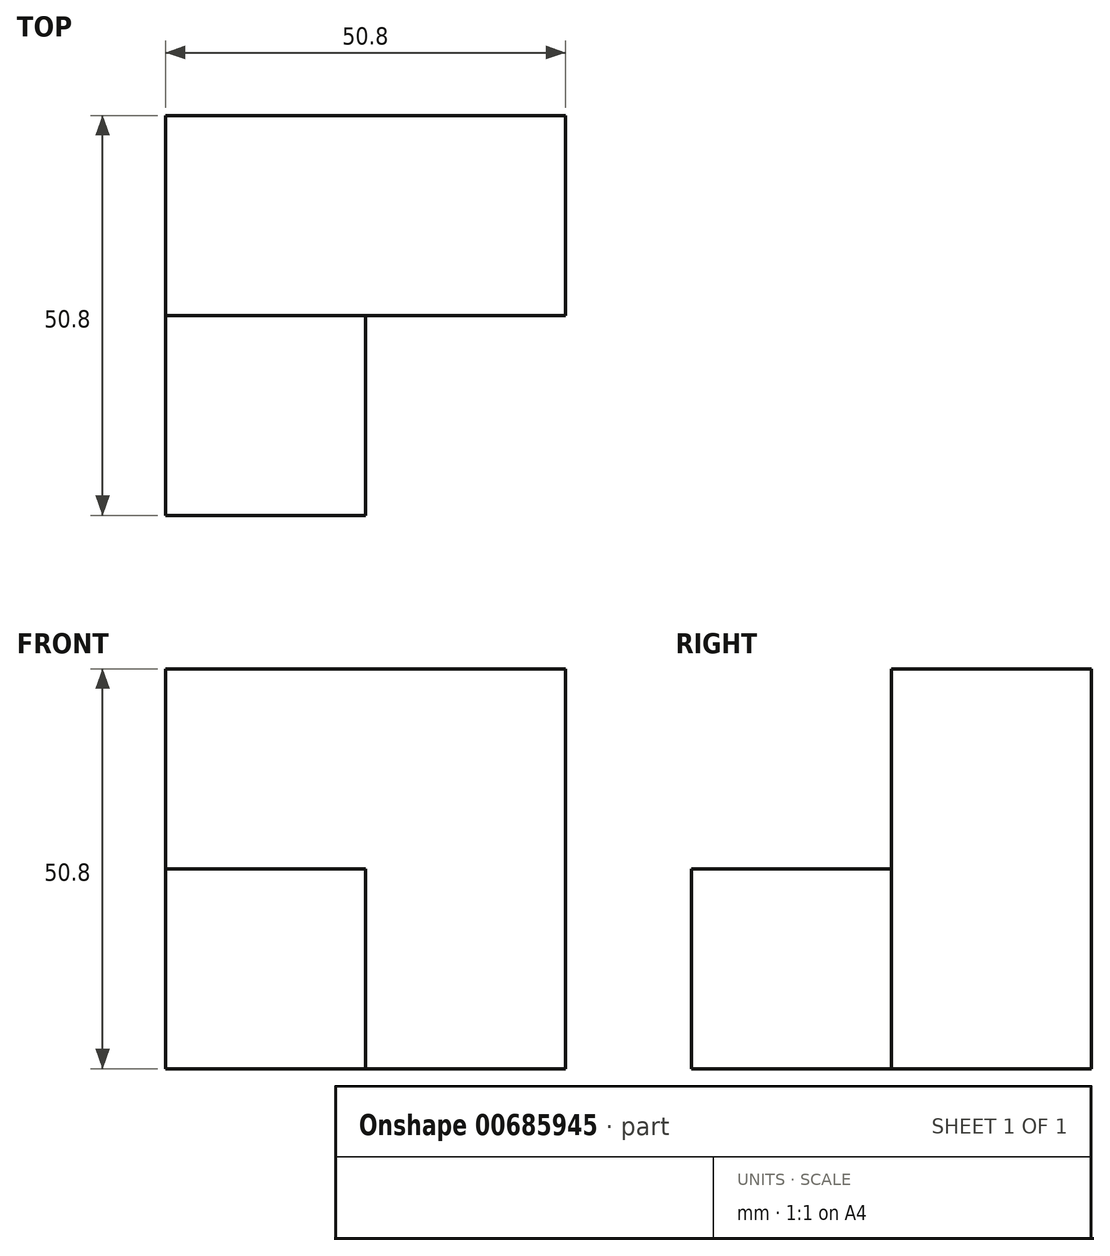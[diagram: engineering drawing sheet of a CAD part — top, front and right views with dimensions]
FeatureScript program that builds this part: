
annotation { "Feature Type Name" : "Feature", "Feature Type Description" : "" }
export const myFeature = defineFeature(function(context is Context, id is Id, definition is map)
    precondition{}
    {
        {
            var Q0;
            Q0=qCreatedBy(makeId("Front.planeOp"),FACE);
            var sketch = newSketch(context, id + "F0", { "sketchPlane" : qUnion([Q0])});
            skLineSegment(sketch, "E0.bottom", {"start": v(0, 0) * mm, "end": v(-50.8, 0) * mm});
            skLineSegment(sketch, "E0.top", {"start": v(0, 50.8) * mm, "end": v(-50.8, 50.8) * mm});
            skLineSegment(sketch, "E0.left", {"start": v(0, 0) * mm, "end": v(0, 50.8) * mm});
            skLineSegment(sketch, "E0.right", {"start": v(-50.8, 0) * mm, "end": v(-50.8, 50.8) * mm});
            skLineSegment(sketch, "E1", {"start": v(0, 50.8) * mm, "end": v(0, 50.8) * mm});
            skSolve(sketch);
        }
        {
            var Q0;
            Q0=makeQuery(id+"F0.imprint","IMPRINT",FACE,{"disambiguationData":[TD([[makeQuery(id+"F0.imprint","IMPRINT",EDGE,{"derivedFrom":sQuery(id+"F0.wireOp",EDGE,"E0.bottom")}),-1.0]])]});
            extrude(context, id + "F1", {"entities" : qUnion([Q0]), "depth" : 25.4 * mm, "offsetDistance" : 25.4 * mm});
        }
        {
            var Q0;
            Q0=makeQuery(id+"F1.opExtrude","CAP_FACE",FACE,{"disambiguationData":[OSD([sQuery(id+"F0.wireOp",EDGE,"E0.bottom"),sQuery(id+"F0.wireOp",EDGE,"E0.top"),sQuery(id+"F0.wireOp",EDGE,"E0.left"),sQuery(id+"F0.wireOp",EDGE,"E0.right")])],"isStart":false});
            var sketch = newSketch(context, id + "F2", { "sketchPlane" : qUnion([Q0])});
            skLineSegment(sketch, "E2.bottom", {"start": v(-50.8, 0) * mm, "end": v(-25.4, 0) * mm});
            skLineSegment(sketch, "E2.top", {"start": v(-50.8, 25.4) * mm, "end": v(-25.4, 25.4) * mm});
            skLineSegment(sketch, "E2.left", {"start": v(-50.8, 0) * mm, "end": v(-50.8, 25.4) * mm});
            skLineSegment(sketch, "E2.right", {"start": v(-25.4, 0) * mm, "end": v(-25.4, 25.4) * mm});
            skSolve(sketch);
        }
        {
            var Q0;
            Q0=makeQuery(id+"F2.imprint","IMPRINT",FACE,{"disambiguationData":[TD([[makeQuery(id+"F2.imprint","IMPRINT",EDGE,{"derivedFrom":sQuery(id+"F2.wireOp",EDGE,"E2.bottom")}),-1.0]])]});
            extrude(context, id + "F3", {"entities" : qUnion([Q0]), "operationType" : NewBodyOperationType.ADD, "depth" : 25.4 * mm, "offsetDistance" : 25.4 * mm});
        }
    });
